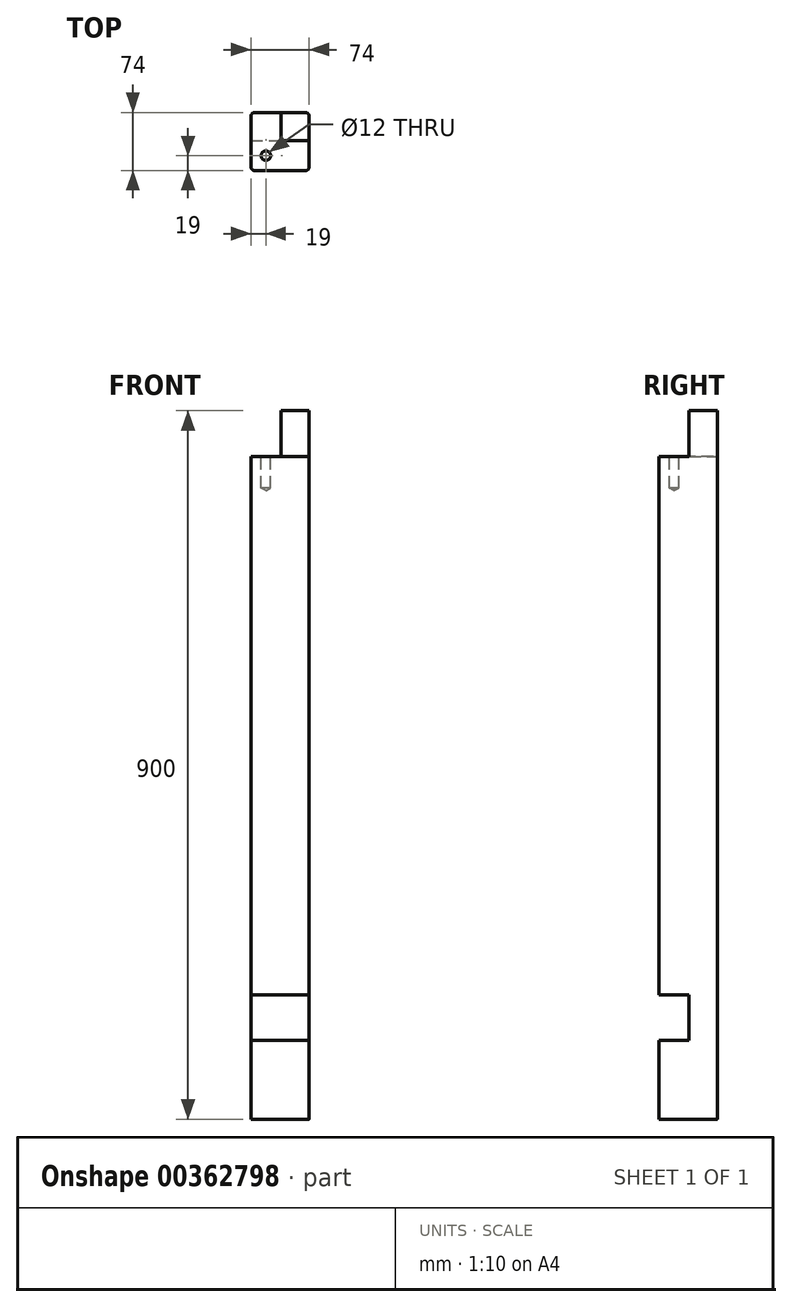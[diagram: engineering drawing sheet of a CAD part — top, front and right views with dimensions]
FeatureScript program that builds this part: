
annotation { "Feature Type Name" : "Feature", "Feature Type Description" : "" }
export const myFeature = defineFeature(function(context is Context, id is Id, definition is map)
    precondition{}
    {
        {
            var Q0;
            Q0=qCreatedBy(makeId("Top.planeOp"),FACE);
            var sketch = newSketch(context, id + "F0", { "sketchPlane" : qUnion([Q0])});
            skLineSegment(sketch, "E0.bottom", {"start": v(37, 37) * mm, "end": v(-37, 37) * mm});
            skLineSegment(sketch, "E0.top", {"start": v(37, -37) * mm, "end": v(-37, -37) * mm});
            skLineSegment(sketch, "E0.left", {"start": v(37, 37) * mm, "end": v(37, -37) * mm});
            skLineSegment(sketch, "E0.right", {"start": v(-37, 37) * mm, "end": v(-37, -37) * mm});
            skPoint(sketch, "E0.middle", {"position": v(0, 0) * mm});
            skSolve(sketch);
        }
        {
            var Q0;
            Q0=makeQuery(id+"F0.imprint","IMPRINT",FACE,{"disambiguationData":[TD([[makeQuery(id+"F0.imprint","IMPRINT",EDGE,{"derivedFrom":sQuery(id+"F0.wireOp",EDGE,"E0.bottom")}),1.0]])]});
            extrude(context, id + "F1", {"entities" : qUnion([Q0]), "oppositeDirection" : true, "depth" : 900 * mm});
        }
        {
            var Q0;
            Q0=makeQuery(id+"F1.opExtrude","SWEPT_FACE",FACE,{"disambiguationData":[OSD([sQuery(id+"F0.wireOp",EDGE,"E0.top")])]});
            var sketch = newSketch(context, id + "F2", { "sketchPlane" : qUnion([Q0])});
            skLineSegment(sketch, "E1", {"start": v(-37, -58) * mm, "end": v(37, -58) * mm});
            skSolve(sketch);
        }
        {
            var Q0;
            Q0=makeQuery(id+"F1.opExtrude","SWEPT_FACE",FACE,{"disambiguationData":[OSD([sQuery(id+"F0.wireOp",EDGE,"E0.right")])]});
            var sketch = newSketch(context, id + "F3", { "sketchPlane" : qUnion([Q0])});
            skLineSegment(sketch, "E2", {"start": v(37, -58) * mm, "end": v(-37, -58) * mm});
            skSolve(sketch);
        }
        {
            var Q0;
            {var subQ0=sQuery(id+"F2.wireOp",EDGE,"E1");Q0=makeQuery(id+"F2.imprint","IMPRINT",FACE,{"disambiguationData":[TD([[makeQuery(id+"F2.imprint","IMPRINT",EDGE,{"derivedFrom":subQ0}),1.0]])]});}
            extrude(context, id + "F4", {"entities" : qUnion([Q0]), "operationType" : NewBodyOperationType.REMOVE, "oppositeDirection" : true, "depth" : 38 * mm});
        }
        {
            var Q0;
            {var subQ0=sQuery(id+"F3.wireOp",EDGE,"E2");Q0=makeQuery(id+"F3.imprint","IMPRINT",FACE,{"disambiguationData":[TD([[makeQuery(id+"F3.imprint","IMPRINT",EDGE,{"derivedFrom":subQ0}),-1.0]])]});}
            extrude(context, id + "F5", {"entities" : qUnion([Q0]), "operationType" : NewBodyOperationType.REMOVE, "oppositeDirection" : true, "depth" : 38 * mm});
        }
        {
            var Q0;
            Q0=makeQuery(id+"F5.boolean.opBoolean","MERGE",FACE,{"derivedFrom":[makeQuery(id+"F4.boolean.opBoolean","COPY",FACE,{"derivedFrom":makeQuery(id+"F4.opExtrude","SWEPT_FACE",FACE,{"disambiguationData":[OSD([sQuery(id+"F2.wireOp",EDGE,"E1")])]})}),makeQuery(id+"F5.opExtrude","SWEPT_FACE",FACE,{"disambiguationData":[OSD([sQuery(id+"F3.wireOp",EDGE,"E2")])]})]});
            var sketch = newSketch(context, id + "F6", { "sketchPlane" : qUnion([Q0])});
            skPoint(sketch, "E3", {"position": v(-18, -18) * mm});
            skSolve(sketch);
        }
        {
            var Q0;
            Q0=sQuery(id+"F6.wireOp",VERTEX,"E3");
            var Q1;
            Q1=makeQuery(id+"F1.opExtrude","SWEPT_BODY",BODY,{"disambiguationData":[OSD([sQuery(id+"F0.wireOp",EDGE,"E0.bottom"),sQuery(id+"F0.wireOp",EDGE,"E0.top"),sQuery(id+"F0.wireOp",EDGE,"E0.left"),sQuery(id+"F0.wireOp",EDGE,"E0.right")])]});
            hole(context, id + "F7", {"style" : HoleStyle.SIMPLE, "endStyle" : HoleEndStyle.BLIND, "holeDiameter" : 12 * mm, "holeDepth" : 40 * mm, "isTappedThrough" : true, "tappedDepth" : 12 * mm, "tapClearance" : 3, "locations" : qUnion([Q0]), "scope" : qUnion([Q1])});
        }
        {
            var Q0;
            Q0=makeQuery(id+"F1.opExtrude","SWEPT_FACE",FACE,{"disambiguationData":[OSD([sQuery(id+"F0.wireOp",EDGE,"E0.top")])]});
            var sketch = newSketch(context, id + "F8", { "sketchPlane" : qUnion([Q0])});
            skLineSegment(sketch, "E4", {"start": v(-37, -800) * mm, "end": v(37, -800) * mm});
            skLineSegment(sketch, "E5", {"start": v(-37, -742) * mm, "end": v(37, -742) * mm});
            skSolve(sketch);
        }
        {
            var Q0;
            {var subQ0=sQuery(id+"F8.wireOp",EDGE,"E4");Q0=makeQuery(id+"F8.imprint","IMPRINT",FACE,{"disambiguationData":[TD([[makeQuery(id+"F8.imprint","IMPRINT",EDGE,{"derivedFrom":subQ0}),1.0]])]});}
            extrude(context, id + "F9", {"entities" : qUnion([Q0]), "operationType" : NewBodyOperationType.REMOVE, "oppositeDirection" : true, "depth" : 38 * mm});
        }
        {
            var Q0;
            Q0=makeQuery(id+"F1.opExtrude","SWEPT_EDGE",EDGE,{"disambiguationData":[OSD([sQuery(id+"F0.wireOp",EDGE,"E0.top"),sQuery(id+"F0.wireOp",EDGE,"E0.right")])]});
            var Q1;
            Q1=makeQuery(id+"F1.opExtrude","SWEPT_EDGE",EDGE,{"disambiguationData":[OSD([sQuery(id+"F0.wireOp",EDGE,"E0.bottom"),sQuery(id+"F0.wireOp",EDGE,"E0.right")])]});
            var Q2;
            Q2=makeQuery(id+"F1.opExtrude","SWEPT_EDGE",EDGE,{"disambiguationData":[OSD([sQuery(id+"F0.wireOp",EDGE,"E0.top"),sQuery(id+"F0.wireOp",EDGE,"E0.left")])]});
            var Q3;
            Q3=makeQuery(id+"F1.opExtrude","SWEPT_EDGE",EDGE,{"disambiguationData":[OSD([sQuery(id+"F0.wireOp",EDGE,"E0.bottom"),sQuery(id+"F0.wireOp",EDGE,"E0.left")])]});
            fillet(context, id + "F10", {"entities" : qUnion([Q0, Q1, Q2, Q3]), "radius" : 5 * mm, "tangentPropagation" : true, "allowEdgeOverflow" : false});
        }
    });
